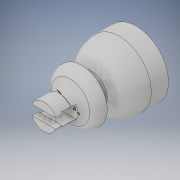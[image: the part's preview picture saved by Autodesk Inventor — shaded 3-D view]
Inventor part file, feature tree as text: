
AUTODESK INVENTOR PART (.ipt)
format: ipt  version: 2018 (Build 220112000, 112)  size: 207,872 bytes
history: native  units: mm
features: sketch x11, extrude x10, fillet x3
ambient origin geometry x8: Origin, YZ Plane, XZ Plane, XY Plane, X Axis, Y Axis, Z Axis, Center Point
bodies: Volumenkörper1 (feature_tree)
feature tree (24):
  extrude  "Extrusion1"  Depth=2.0mm TaperAngle=0.0deg
  fillet  "Rundung1"  Radius=2.0mm
  extrude  "Extrusion2"  Depth=1.5mm TaperAngle=0.0deg
  extrude  "Extrusion3"  Depth=10.0mm TaperAngle=0.0deg
  extrude  "Extrusion5"  Depth=2.0mm TaperAngle=0.0deg
  extrude  "Extrusion6"  Depth=2.0mm TaperAngle=0.0deg
  extrude  "Extrusion7"  Depth=1.1mm TaperAngle=0.0deg
  fillet  "Rundung2"  Radius=5.0mm
  sketch  "Skizze11"  dims[d23=4.0mm d24=4.0mm]
  extrude  "Extrusion8"  Depth=4.0mm
  extrude  "Extrusion9"  Depth=2.15mm TaperAngle=0.0deg
  extrude  "Extrusion10"  Depth=4.0mm TaperAngle=0.0deg
  extrude  "Extrusion11"  Depth=2.0mm
  fillet  "Rundung3"  [1 undecoded]
  sketch  "Skizze1"  dims[d0=8.0mm d1=2.0mm d2=0.0mm d3=2.0mm]
  sketch  "Skizze2"  dims[d4=5.0mm d5=1.5mm d6=0.0mm]
  sketch  "Skizze3"  dims[d7=10.0mm d8=5.0mm d9=0.0mm]
  sketch  "Skizze5"  dims[d13=10.0mm d14=2.0mm d15=0.0mm]
  sketch  "Skizze6"  dims[d16=8.5mm d17=2.0mm d18=0.0mm]
  sketch  "Skizze8"  dims[d19=1.6mm d20=1.1mm d21=0.0mm d22=5.0mm]
  sketch  "Skizze12"  dims[d25=2.85mm d26=0.0mm d27=2.15mm d28=0.0mm]
  sketch  "Skizze13"  dims[d29=4.0mm d30=1.0mm d31=0.0mm]
  sketch  "Skizze14"  dims[d32=1.0mm d33=0.0mm d34=2.0mm]
  sketch  "Skizze15"
note: 1 required parameter value undecoded (feature->parameter linkage not recoverable at this tier; creation-order binding heuristic only, values carry confidence <= 0.55)
